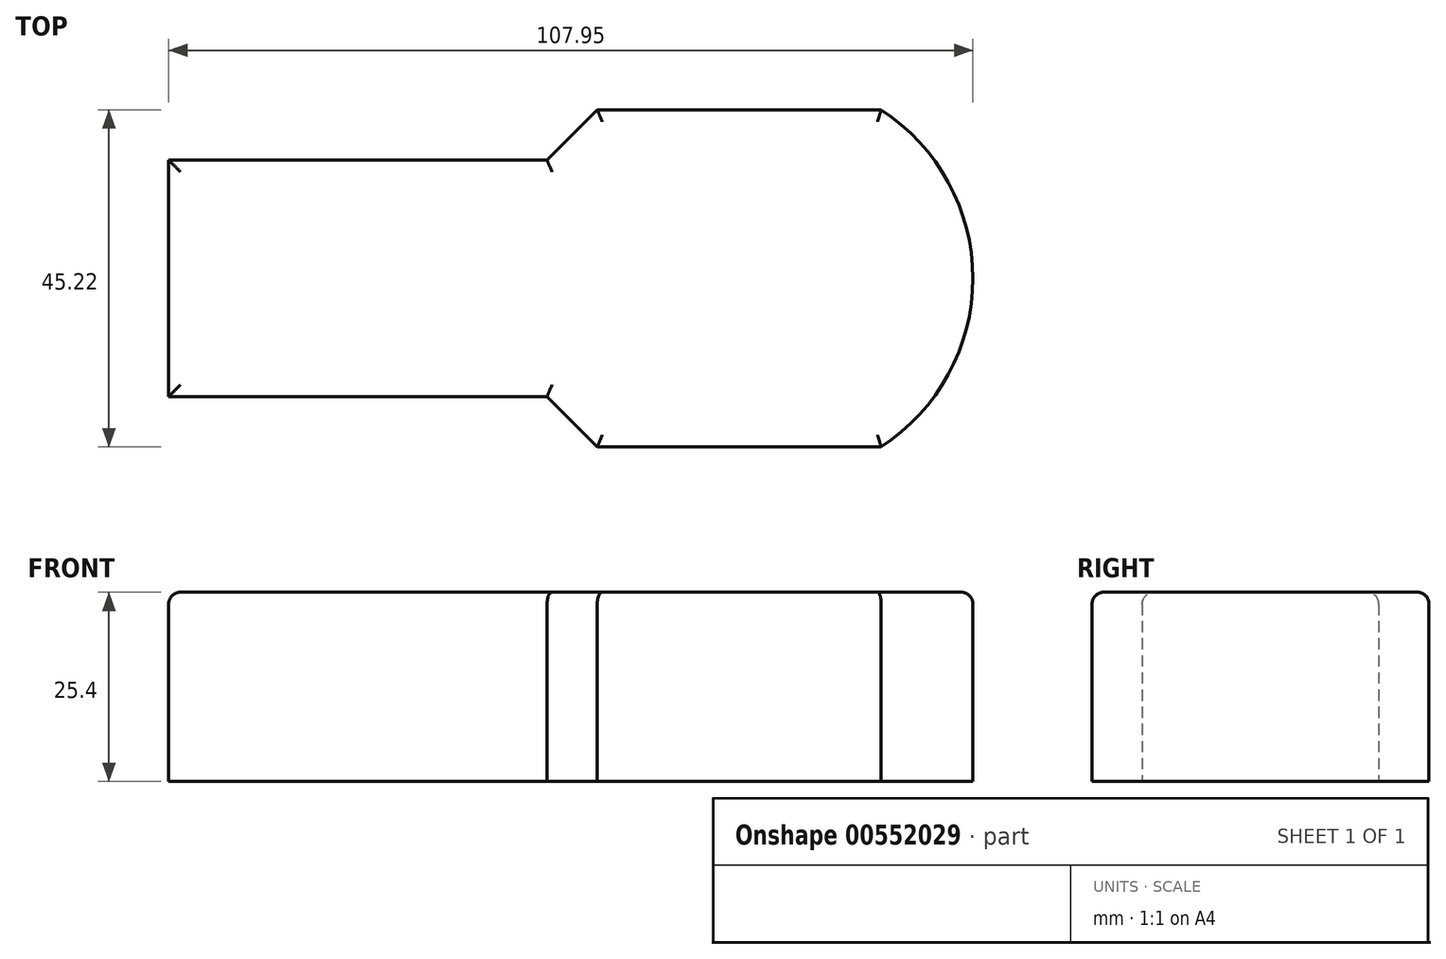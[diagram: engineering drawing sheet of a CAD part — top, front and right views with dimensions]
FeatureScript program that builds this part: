
annotation { "Feature Type Name" : "Feature", "Feature Type Description" : "" }
export const myFeature = defineFeature(function(context is Context, id is Id, definition is map)
    precondition{}
    {
        {
            var Q0;
            Q0=qCreatedBy(makeId("Top.planeOp"),FACE);
            var sketch = newSketch(context, id + "F0", { "sketchPlane" : qUnion([Q0])});
            skLineSegment(sketch, "E0", {"start": v(-41.11, -15.44) * mm, "end": v(9.69, -15.44) * mm});
            skLineSegment(sketch, "E1", {"start": v(9.69, -15.44) * mm, "end": v(16.42, -22.18) * mm});
            skLineSegment(sketch, "E2", {"start": v(16.42, -22.18) * mm, "end": v(54.52, -22.18) * mm});
            skLineSegment(sketch, "E3", {"start": v(-41.11, -15.44) * mm, "end": v(-41.11, 16.3) * mm});
            skLineSegment(sketch, "E4", {"start": v(-41.11, 16.3) * mm, "end": v(9.69, 16.3) * mm});
            skLineSegment(sketch, "E5", {"start": v(9.69, 16.3) * mm, "end": v(16.42, 23.04) * mm});
            skLineSegment(sketch, "E6", {"start": v(16.42, 23.04) * mm, "end": v(54.52, 23.04) * mm});
            skArc(sketch, "E7", {"start": v(54.52, -22.18) * mm, "mid": v(66.84, 0.43) * mm, "end": v(54.52, 23.04) * mm});
            skSolve(sketch);
        }
        {
            var Q0;
            Q0=makeQuery(id+"F0.imprint","IMPRINT",FACE,{"disambiguationData":[TD([[makeQuery(id+"F0.imprint","IMPRINT",EDGE,{"derivedFrom":sQuery(id+"F0.wireOp",EDGE,"E0")}),1.0]])]});
            extrude(context, id + "F1", {"entities" : qUnion([Q0]), "depth" : 25.4 * mm, "offsetDistance" : 25.4 * mm});
        }
        {
            var Q0;
            Q0=makeQuery(id+"F1.opExtrude","CAP_FACE",FACE,{"disambiguationData":[OSD([sQuery(id+"F0.wireOp",EDGE,"E0"),sQuery(id+"F0.wireOp",EDGE,"E1"),sQuery(id+"F0.wireOp",EDGE,"E2"),sQuery(id+"F0.wireOp",EDGE,"E3"),sQuery(id+"F0.wireOp",EDGE,"E4"),sQuery(id+"F0.wireOp",EDGE,"E5"),sQuery(id+"F0.wireOp",EDGE,"E6"),sQuery(id+"F0.wireOp",EDGE,"E7")])],"isStart":false});
            fillet(context, id + "F2", {"entities" : qUnion([Q0]), "radius" : 1.57 * mm, "tangentPropagation" : true, "allowEdgeOverflow" : false});
        }
    });
